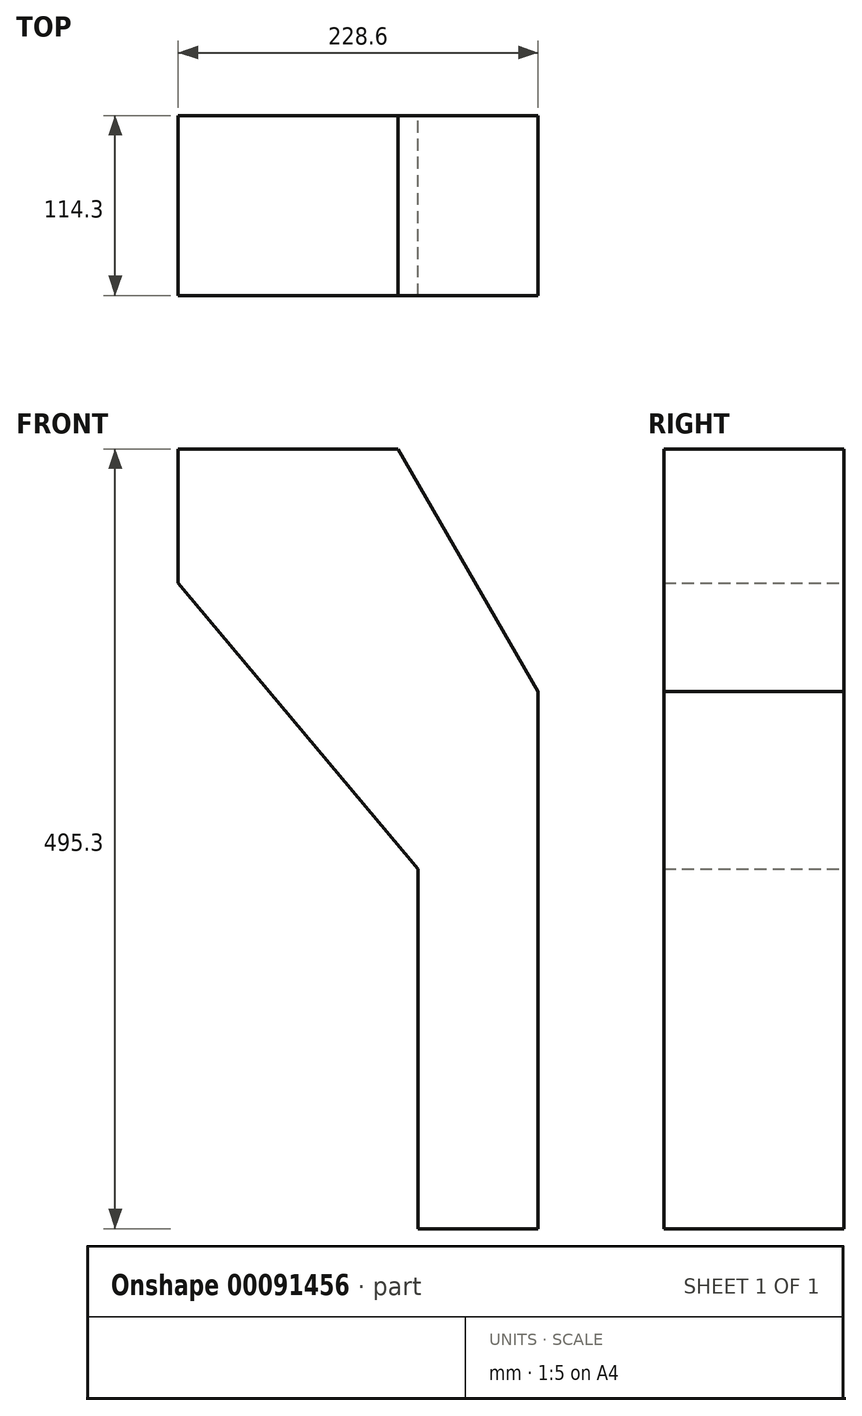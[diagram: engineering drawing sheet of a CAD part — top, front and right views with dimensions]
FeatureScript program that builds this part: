
annotation { "Feature Type Name" : "Feature", "Feature Type Description" : "" }
export const myFeature = defineFeature(function(context is Context, id is Id, definition is map)
    precondition{}
    {
        {
            var Q0;
            Q0=qCreatedBy(makeId("Front.planeOp"),FACE);
            var sketch = newSketch(context, id + "F0", { "sketchPlane" : qUnion([Q0])});
            skLineSegment(sketch, "E0", {"start": v(0, 0) * mm, "end": v(0, -85.08) * mm});
            skLineSegment(sketch, "E1", {"start": v(0, -85.08) * mm, "end": v(152.4, -266.7) * mm});
            skLineSegment(sketch, "E2", {"start": v(152.4, -266.7) * mm, "end": v(152.4, -495.3) * mm});
            skLineSegment(sketch, "E3", {"start": v(152.4, -495.3) * mm, "end": v(228.6, -495.3) * mm});
            skLineSegment(sketch, "E4", {"start": v(228.6, -495.3) * mm, "end": v(228.6, -153.98) * mm});
            skLineSegment(sketch, "E5", {"start": v(228.6, -153.98) * mm, "end": v(139.7, 0) * mm});
            skLineSegment(sketch, "E6", {"start": v(139.7, 0) * mm, "end": v(0, 0) * mm});
            skSolve(sketch);
        }
        {
            var Q0;
            Q0 = qSketchRegion(id + "F0", true);
            extrude(context, id + "F1", {"entities" : qUnion([Q0]), "endBound" : BoundingType.SYMMETRIC, "depth" : 114.3 * mm});
        }
    });
